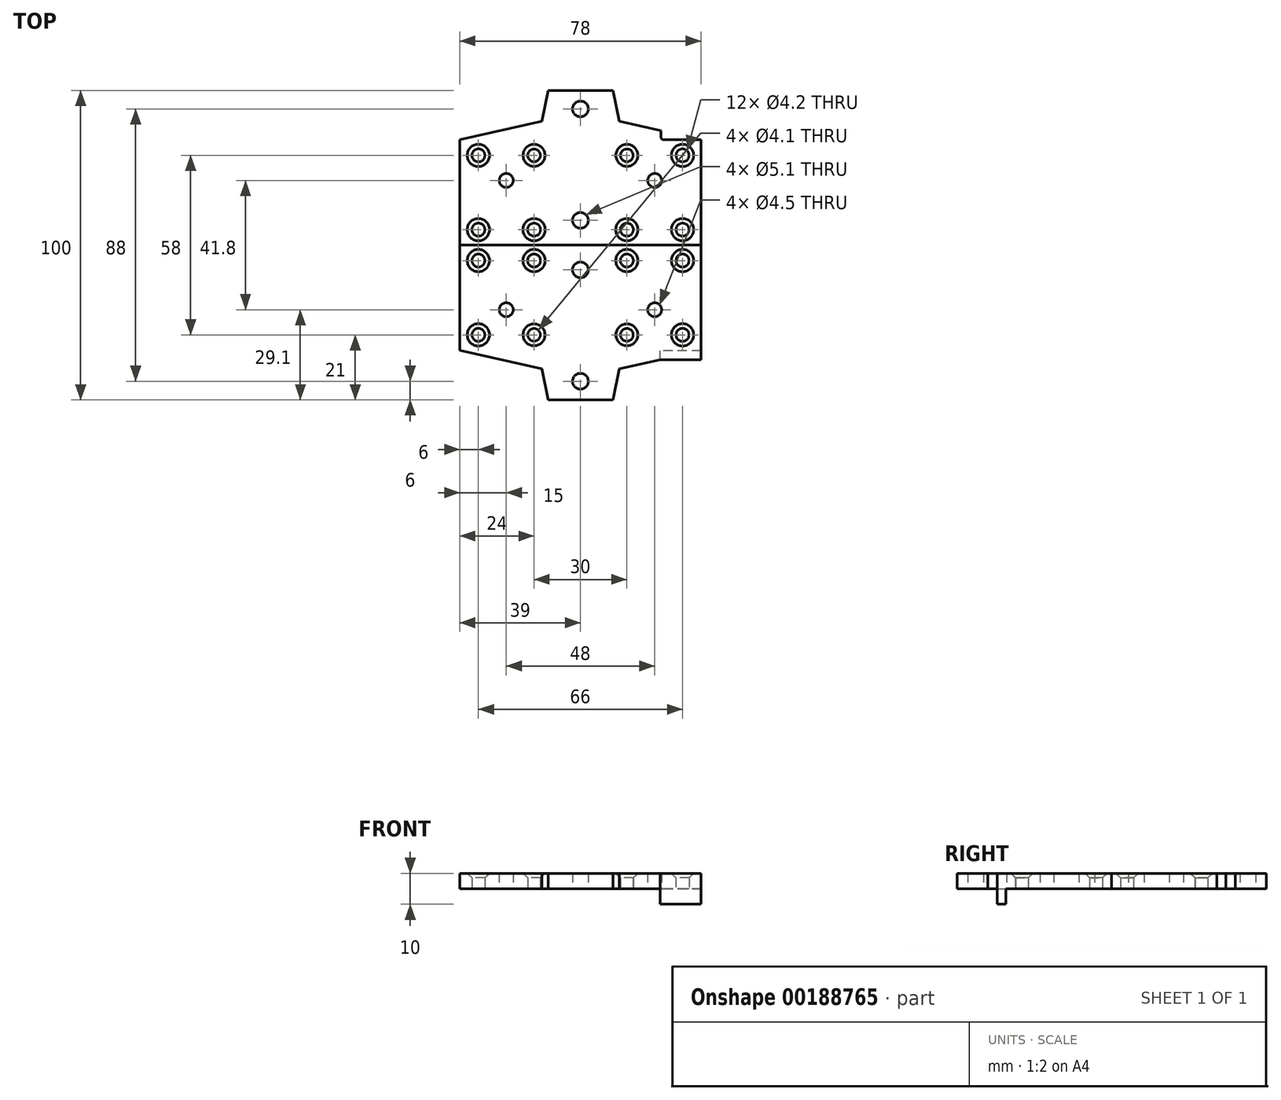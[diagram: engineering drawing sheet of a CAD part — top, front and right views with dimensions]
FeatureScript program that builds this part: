
annotation { "Feature Type Name" : "Feature", "Feature Type Description" : "" }
export const myFeature = defineFeature(function(context is Context, id is Id, definition is map)
    precondition{}
    {
        {
            var Q0;
            Q0=qCreatedBy(makeId("Top.planeOp"),FACE);
            var sketch = newSketch(context, id + "F0", { "sketchPlane" : qUnion([Q0])});
            skLineSegment(sketch, "E0.bottom", {"start": v(39, -17) * mm, "end": v(-39, -17) * mm});
            skLineSegment(sketch, "E0.top", {"start": v(39, 17) * mm, "end": v(-39, 17) * mm});
            skLineSegment(sketch, "E0.left", {"start": v(39, -17) * mm, "end": v(39, 17) * mm});
            skLineSegment(sketch, "E0.right", {"start": v(-39, -17) * mm, "end": v(-39, 17) * mm});
            skPoint(sketch, "E0.middle", {"position": v(0, 0) * mm});
            skLineSegment(sketch, "E1", {"start": v(-10.5, 33) * mm, "end": v(10.5, 33) * mm});
            skLineSegment(sketch, "E2", {"start": v(0, -17) * mm, "end": v(0, 41.6) * mm, "construction": true});
            skLineSegment(sketch, "E3", {"start": v(33, -17) * mm, "end": v(33, 17) * mm, "construction": true});
            skLineSegment(sketch, "E4", {"start": v(-33, -17) * mm, "end": v(-33, 17) * mm, "construction": true});
            skLineSegment(sketch, "E5", {"start": v(-39, -12) * mm, "end": v(39, -12) * mm, "construction": true});
            skLineSegment(sketch, "E6", {"start": v(-39, 12) * mm, "end": v(39, 12) * mm, "construction": true});
            skCircle(sketch, "E7", {"center": v(33, 12) * mm, "radius": 2.1 * mm});
            skCircle(sketch, "E8", {"center": v(33, -12) * mm, "radius": 2.1 * mm});
            skCircle(sketch, "E9", {"center": v(-33, -12) * mm, "radius": 2.1 * mm});
            skCircle(sketch, "E10", {"center": v(-33, 12) * mm, "radius": 2.1 * mm});
            skCircle(sketch, "E11", {"center": v(-15, 12) * mm, "radius": 2.05 * mm});
            skCircle(sketch, "E12", {"center": v(-15, -12) * mm, "radius": 2.1 * mm});
            skCircle(sketch, "E13", {"center": v(15, 12) * mm, "radius": 2.05 * mm});
            skCircle(sketch, "E14", {"center": v(15, -12) * mm, "radius": 2.1 * mm});
            skCircle(sketch, "E15", {"center": v(0, 27) * mm, "radius": 2.55 * mm});
            skCircle(sketch, "E16", {"center": v(0, -9) * mm, "radius": 2.55 * mm});
            skCircle(sketch, "E17", {"center": v(24, 3.9) * mm, "radius": 2.25 * mm});
            skCircle(sketch, "E18", {"center": v(-24, 3.9) * mm, "radius": 2.25 * mm});
            skLineSegment(sketch, "E19", {"start": v(-10.5, 33) * mm, "end": v(-12.5, 23) * mm});
            skLineSegment(sketch, "E20", {"start": v(-12.5, 23) * mm, "end": v(-39, 17) * mm});
            skLineSegment(sketch, "E21", {"start": v(10.5, 33) * mm, "end": v(12.5, 23) * mm});
            skLineSegment(sketch, "E22", {"start": v(12.5, 23) * mm, "end": v(39, 17) * mm});
            skSolve(sketch);
        }
        {
            var Q0;
            Q0=makeQuery(id+"F0.imprint","IMPRINT",FACE,{"disambiguationData":[TD([[makeQuery(id+"F0.imprint","IMPRINT",EDGE,{"derivedFrom":sQuery(id+"F0.wireOp",EDGE,"E0.bottom")}),-1.0]])]});
            var Q1;
            Q1=makeQuery(id+"F0.imprint","IMPRINT",FACE,{"disambiguationData":[TD([[makeQuery(id+"F0.imprint","IMPRINT",EDGE,{"derivedFrom":sQuery(id+"F0.wireOp",EDGE,"E0.top")}),-1.0]])]});
            extrude(context, id + "F1", {"entities" : qUnion([Q0, Q1]), "depth" : 5 * mm, "offsetDistance" : 25 * mm});
        }
        {
            var Q0;
            Q0=makeQuery(id+"F1.opExtrude","CAP_EDGE",EDGE,{"disambiguationData":[OSD([sQuery(id+"F0.wireOp",EDGE,"E9")])],"isStart":false});
            var Q1;
            Q1=makeQuery(id+"F1.opExtrude","CAP_EDGE",EDGE,{"disambiguationData":[OSD([sQuery(id+"F0.wireOp",EDGE,"E10")])],"isStart":false});
            var Q2;
            Q2=makeQuery(id+"F1.opExtrude","CAP_EDGE",EDGE,{"disambiguationData":[OSD([sQuery(id+"F0.wireOp",EDGE,"E12")])],"isStart":false});
            var Q3;
            Q3=makeQuery(id+"F1.opExtrude","CAP_EDGE",EDGE,{"disambiguationData":[OSD([sQuery(id+"F0.wireOp",EDGE,"E11")])],"isStart":false});
            var Q4;
            Q4=makeQuery(id+"F1.opExtrude","CAP_EDGE",EDGE,{"disambiguationData":[OSD([sQuery(id+"F0.wireOp",EDGE,"E14")])],"isStart":false});
            var Q5;
            Q5=makeQuery(id+"F1.opExtrude","CAP_EDGE",EDGE,{"disambiguationData":[OSD([sQuery(id+"F0.wireOp",EDGE,"E8")])],"isStart":false});
            var Q6;
            Q6=makeQuery(id+"F1.opExtrude","CAP_EDGE",EDGE,{"disambiguationData":[OSD([sQuery(id+"F0.wireOp",EDGE,"E13")])],"isStart":false});
            var Q7;
            Q7=makeQuery(id+"F1.opExtrude","CAP_EDGE",EDGE,{"disambiguationData":[OSD([sQuery(id+"F0.wireOp",EDGE,"E7")])],"isStart":false});
            chamfer(context, id + "F2", {"entities" : qUnion([Q0, Q1, Q2, Q3, Q4, Q5, Q6, Q7]), "width" : 1.5 * mm, "tangentPropagation" : true});
        }
        {
            var Q0;
            Q0=makeQuery(id+"F1.opExtrude","SWEPT_BODY",BODY,{"disambiguationData":[OSD([sQuery(id+"F0.wireOp",EDGE,"E0.bottom"),sQuery(id+"F0.wireOp",EDGE,"E0.left"),sQuery(id+"F0.wireOp",EDGE,"E0.right"),sQuery(id+"F0.wireOp",EDGE,"E1"),sQuery(id+"F0.wireOp",EDGE,"E7"),sQuery(id+"F0.wireOp",EDGE,"E8"),sQuery(id+"F0.wireOp",EDGE,"E9"),sQuery(id+"F0.wireOp",EDGE,"E10"),sQuery(id+"F0.wireOp",EDGE,"E11"),sQuery(id+"F0.wireOp",EDGE,"E12"),sQuery(id+"F0.wireOp",EDGE,"E13"),sQuery(id+"F0.wireOp",EDGE,"E14"),sQuery(id+"F0.wireOp",EDGE,"E15"),sQuery(id+"F0.wireOp",EDGE,"E16"),sQuery(id+"F0.wireOp",EDGE,"E17"),sQuery(id+"F0.wireOp",EDGE,"E18"),sQuery(id+"F0.wireOp",EDGE,"E19"),sQuery(id+"F0.wireOp",EDGE,"E20"),sQuery(id+"F0.wireOp",EDGE,"E21"),sQuery(id+"F0.wireOp",EDGE,"E22")])]});
            var Q1;
            Q1=makeQuery(id+"F1.opExtrude","SWEPT_FACE",FACE,{"disambiguationData":[OSD([sQuery(id+"F0.wireOp",EDGE,"E0.bottom")])]});
            mirror(context, id + "F3", {"entities" : qUnion([Q0]), "mirrorPlane" : qUnion([Q1])});
        }
        {
            var Q0;
            Q0=makeQuery(id+"F3.opPattern","COPY",FACE,{"derivedFrom":makeQuery(id+"F1.opExtrude","CAP_FACE",FACE,{"disambiguationData":[OSD([sQuery(id+"F0.wireOp",EDGE,"E0.bottom"),sQuery(id+"F0.wireOp",EDGE,"E0.left"),sQuery(id+"F0.wireOp",EDGE,"E0.right"),sQuery(id+"F0.wireOp",EDGE,"E1"),sQuery(id+"F0.wireOp",EDGE,"E7"),sQuery(id+"F0.wireOp",EDGE,"E8"),sQuery(id+"F0.wireOp",EDGE,"E9"),sQuery(id+"F0.wireOp",EDGE,"E10"),sQuery(id+"F0.wireOp",EDGE,"E11"),sQuery(id+"F0.wireOp",EDGE,"E12"),sQuery(id+"F0.wireOp",EDGE,"E13"),sQuery(id+"F0.wireOp",EDGE,"E14"),sQuery(id+"F0.wireOp",EDGE,"E15"),sQuery(id+"F0.wireOp",EDGE,"E16"),sQuery(id+"F0.wireOp",EDGE,"E17"),sQuery(id+"F0.wireOp",EDGE,"E18"),sQuery(id+"F0.wireOp",EDGE,"E19"),sQuery(id+"F0.wireOp",EDGE,"E20"),sQuery(id+"F0.wireOp",EDGE,"E21"),sQuery(id+"F0.wireOp",EDGE,"E22")])],"isStart":false}),"instanceName":"1"});
            var sketch = newSketch(context, id + "F4", { "sketchPlane" : qUnion([Q0])});
            skLineSegment(sketch, "E23", {"start": v(25.75, -54) * mm, "end": v(39, -54) * mm});
            skLineSegment(sketch, "E24", {"start": v(39, -54) * mm, "end": v(39, -51) * mm});
            skSolve(sketch);
        }
        {
            var Q0;
            {var subQ0=sQuery(id+"F4.wireOp",EDGE,"E23");Q0=makeQuery(id+"F4.imprint","IMPRINT",FACE,{"disambiguationData":[TD([[makeQuery(id+"F4.imprint","IMPRINT",EDGE,{"derivedFrom":subQ0}),1.0]])]});}
            var Q1;
            Q1=makeQuery(id+"F3.opPattern","COPY",FACE,{"derivedFrom":makeQuery(id+"F1.opExtrude","CAP_FACE",FACE,{"disambiguationData":[OSD([sQuery(id+"F0.wireOp",EDGE,"E0.bottom"),sQuery(id+"F0.wireOp",EDGE,"E0.left"),sQuery(id+"F0.wireOp",EDGE,"E0.right"),sQuery(id+"F0.wireOp",EDGE,"E1"),sQuery(id+"F0.wireOp",EDGE,"E7"),sQuery(id+"F0.wireOp",EDGE,"E8"),sQuery(id+"F0.wireOp",EDGE,"E9"),sQuery(id+"F0.wireOp",EDGE,"E10"),sQuery(id+"F0.wireOp",EDGE,"E11"),sQuery(id+"F0.wireOp",EDGE,"E12"),sQuery(id+"F0.wireOp",EDGE,"E13"),sQuery(id+"F0.wireOp",EDGE,"E14"),sQuery(id+"F0.wireOp",EDGE,"E15"),sQuery(id+"F0.wireOp",EDGE,"E16"),sQuery(id+"F0.wireOp",EDGE,"E17"),sQuery(id+"F0.wireOp",EDGE,"E18"),sQuery(id+"F0.wireOp",EDGE,"E19"),sQuery(id+"F0.wireOp",EDGE,"E20"),sQuery(id+"F0.wireOp",EDGE,"E21"),sQuery(id+"F0.wireOp",EDGE,"E22")])],"isStart":true}),"instanceName":"1"});
            extrude(context, id + "F5", {"entities" : qUnion([Q0]), "operationType" : NewBodyOperationType.ADD, "endBound" : BoundingType.UP_TO_SURFACE, "oppositeDirection" : true, "depth" : 25 * mm, "endBoundEntityFace" : qUnion([Q1]), "offsetDistance" : 25 * mm});
        }
        {
            var Q0;
            {var subQ0=sQuery(id+"F0.wireOp",EDGE,"E22");var subQ1=sQuery(id+"F0.wireOp",EDGE,"E21");var subQ2=sQuery(id+"F0.wireOp",EDGE,"E20");var subQ3=sQuery(id+"F0.wireOp",EDGE,"E19");var subQ4=sQuery(id+"F0.wireOp",EDGE,"E18");var subQ5=sQuery(id+"F0.wireOp",EDGE,"E17");var subQ6=sQuery(id+"F0.wireOp",EDGE,"E16");var subQ7=sQuery(id+"F0.wireOp",EDGE,"E15");var subQ8=sQuery(id+"F0.wireOp",EDGE,"E14");var subQ9=sQuery(id+"F0.wireOp",EDGE,"E13");var subQ10=sQuery(id+"F0.wireOp",EDGE,"E12");var subQ11=sQuery(id+"F0.wireOp",EDGE,"E11");var subQ12=sQuery(id+"F0.wireOp",EDGE,"E10");var subQ13=sQuery(id+"F0.wireOp",EDGE,"E9");var subQ14=sQuery(id+"F0.wireOp",EDGE,"E8");var subQ15=sQuery(id+"F0.wireOp",EDGE,"E7");var subQ16=sQuery(id+"F0.wireOp",EDGE,"E1");var subQ17=sQuery(id+"F0.wireOp",EDGE,"E0.right");var subQ18=sQuery(id+"F0.wireOp",EDGE,"E0.left");var subQ19=sQuery(id+"F0.wireOp",EDGE,"E0.bottom");Q0=makeQuery(id+"F5.boolean.opBoolean","MERGE",FACE,{"derivedFrom":[makeQuery(id+"F3.opPattern","COPY",FACE,{"derivedFrom":makeQuery(id+"F1.opExtrude","CAP_FACE",FACE,{"disambiguationData":[OSD([subQ19,subQ18,subQ17,subQ16,subQ15,subQ14,subQ13,subQ12,subQ11,subQ10,subQ9,subQ8,subQ7,subQ6,subQ5,subQ4,subQ3,subQ2,subQ1,subQ0])],"isStart":true}),"instanceName":"1"}),makeQuery(id+"F5.opExtrude","CAP_FACE",FACE,{"disambiguationData":[OSD([subQ19,subQ18,subQ17,subQ16,subQ15,subQ14,subQ13,subQ12,subQ11,subQ10,subQ9,subQ8,subQ7,subQ6,subQ5,subQ4,subQ3,subQ2,subQ1,subQ0])],"isStart":false})]});}
            var sketch = newSketch(context, id + "F6", { "sketchPlane" : qUnion([Q0])});
            skLineSegment(sketch, "E25.bottom", {"start": v(39, 54) * mm, "end": v(25.75, 54) * mm});
            skLineSegment(sketch, "E25.top", {"start": v(39, 51.2) * mm, "end": v(25.75, 51.2) * mm});
            skLineSegment(sketch, "E25.left", {"start": v(39, 54) * mm, "end": v(39, 51.2) * mm});
            skLineSegment(sketch, "E25.right", {"start": v(25.75, 54) * mm, "end": v(25.75, 51.2) * mm});
            skSolve(sketch);
        }
        {
            var Q0;
            Q0=makeQuery(id+"F6.imprint","IMPRINT",FACE,{"disambiguationData":[TD([[makeQuery(id+"F6.imprint","IMPRINT",EDGE,{"derivedFrom":sQuery(id+"F6.wireOp",EDGE,"E25.bottom")}),1.0]])]});
            extrude(context, id + "F7", {"entities" : qUnion([Q0]), "operationType" : NewBodyOperationType.ADD, "depth" : 5 * mm, "offsetDistance" : 25 * mm});
        }
        {
            var Q0;
            Q0=makeQuery(id+"F1.opExtrude","CAP_FACE",FACE,{"disambiguationData":[OSD([sQuery(id+"F0.wireOp",EDGE,"E0.bottom"),sQuery(id+"F0.wireOp",EDGE,"E0.left"),sQuery(id+"F0.wireOp",EDGE,"E0.right"),sQuery(id+"F0.wireOp",EDGE,"E1"),sQuery(id+"F0.wireOp",EDGE,"E7"),sQuery(id+"F0.wireOp",EDGE,"E8"),sQuery(id+"F0.wireOp",EDGE,"E9"),sQuery(id+"F0.wireOp",EDGE,"E10"),sQuery(id+"F0.wireOp",EDGE,"E11"),sQuery(id+"F0.wireOp",EDGE,"E12"),sQuery(id+"F0.wireOp",EDGE,"E13"),sQuery(id+"F0.wireOp",EDGE,"E14"),sQuery(id+"F0.wireOp",EDGE,"E15"),sQuery(id+"F0.wireOp",EDGE,"E16"),sQuery(id+"F0.wireOp",EDGE,"E17"),sQuery(id+"F0.wireOp",EDGE,"E18"),sQuery(id+"F0.wireOp",EDGE,"E19"),sQuery(id+"F0.wireOp",EDGE,"E20"),sQuery(id+"F0.wireOp",EDGE,"E21"),sQuery(id+"F0.wireOp",EDGE,"E22")])],"isStart":false});
            var sketch = newSketch(context, id + "F8", { "sketchPlane" : qUnion([Q0])});
            skLineSegment(sketch, "E26", {"start": v(39, 17) * mm, "end": v(26, 17) * mm});
            skLineSegment(sketch, "E27", {"start": v(26, 17) * mm, "end": v(26, 19.94) * mm});
            skSolve(sketch);
        }
        {
            var Q0;
            {var subQ0=sQuery(id+"F8.wireOp",EDGE,"E26");Q0=makeQuery(id+"F8.imprint","IMPRINT",FACE,{"disambiguationData":[TD([[makeQuery(id+"F8.imprint","IMPRINT",EDGE,{"derivedFrom":subQ0}),-1.0]])]});}
            extrude(context, id + "F9", {"entities" : qUnion([Q0]), "operationType" : NewBodyOperationType.REMOVE, "endBound" : BoundingType.UP_TO_NEXT, "oppositeDirection" : true, "depth" : 25 * mm, "offsetDistance" : 25 * mm});
        }
        {
            var Q0;
            Q0=makeQuery(id+"F9.boolean.opBoolean","COPY",EDGE,{"derivedFrom":makeQuery(id+"F9.opExtrude","SWEPT_EDGE",EDGE,{"disambiguationData":[OSD([sQuery(id+"F0.wireOp",EDGE,"E22"),sQuery(id+"F8.wireOp",EDGE,"E27")])]})});
            var Q1;
            Q1=makeQuery(id+"F9.boolean.opBoolean","COPY",EDGE,{"derivedFrom":makeQuery(id+"F9.opExtrude","SWEPT_EDGE",EDGE,{"disambiguationData":[OSD([sQuery(id+"F8.wireOp",EDGE,"E26"),sQuery(id+"F8.wireOp",EDGE,"E27")])]})});
            fillet(context, id + "F10", {"entities" : qUnion([Q0, Q1]), "radius" : 1 * mm, "tangentPropagation" : true, "allowEdgeOverflow" : false});
        }
    });
